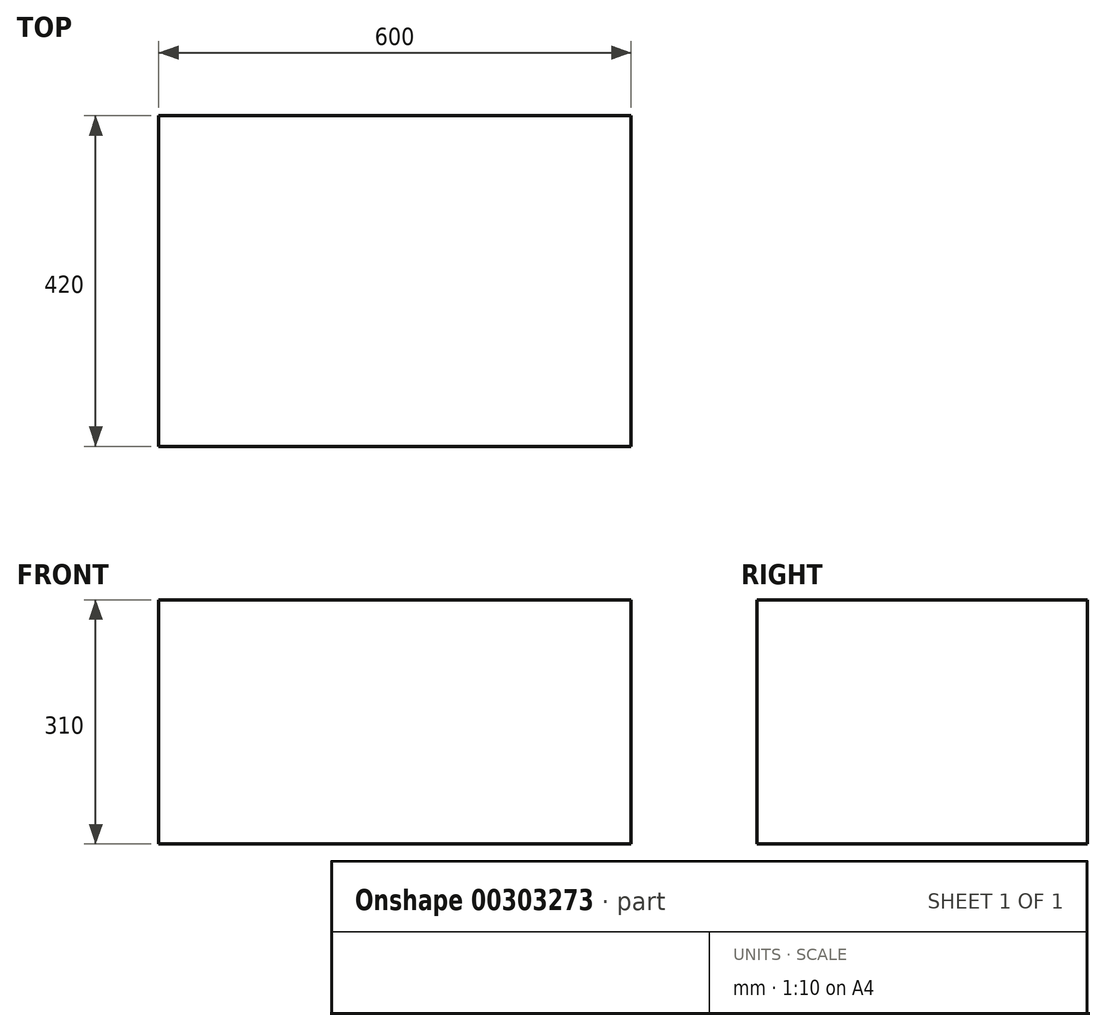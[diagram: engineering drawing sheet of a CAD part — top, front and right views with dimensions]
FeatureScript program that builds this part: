
annotation { "Feature Type Name" : "Feature", "Feature Type Description" : "" }
export const myFeature = defineFeature(function(context is Context, id is Id, definition is map)
    precondition{}
    {
        {
            var Q0;
            Q0=qCreatedBy(makeId("Front.planeOp"),FACE);
            var sketch = newSketch(context, id + "F0", { "sketchPlane" : qUnion([Q0])});
            skLineSegment(sketch, "E0.bottom", {"start": v(-300, 310) * mm, "end": v(300, 310) * mm});
            skLineSegment(sketch, "E0.top", {"start": v(-300, 0) * mm, "end": v(300, 0) * mm});
            skLineSegment(sketch, "E0.left", {"start": v(-300, 310) * mm, "end": v(-300, 0) * mm});
            skLineSegment(sketch, "E0.right", {"start": v(300, 310) * mm, "end": v(300, 0) * mm});
            skSolve(sketch);
        }
        {
            var Q0;
            Q0 = qSketchRegion(id + "F0", true);
            extrude(context, id + "F1", {"entities" : qUnion([Q0]), "endBound" : BoundingType.SYMMETRIC, "depth" : 420 * mm});
        }
    });
